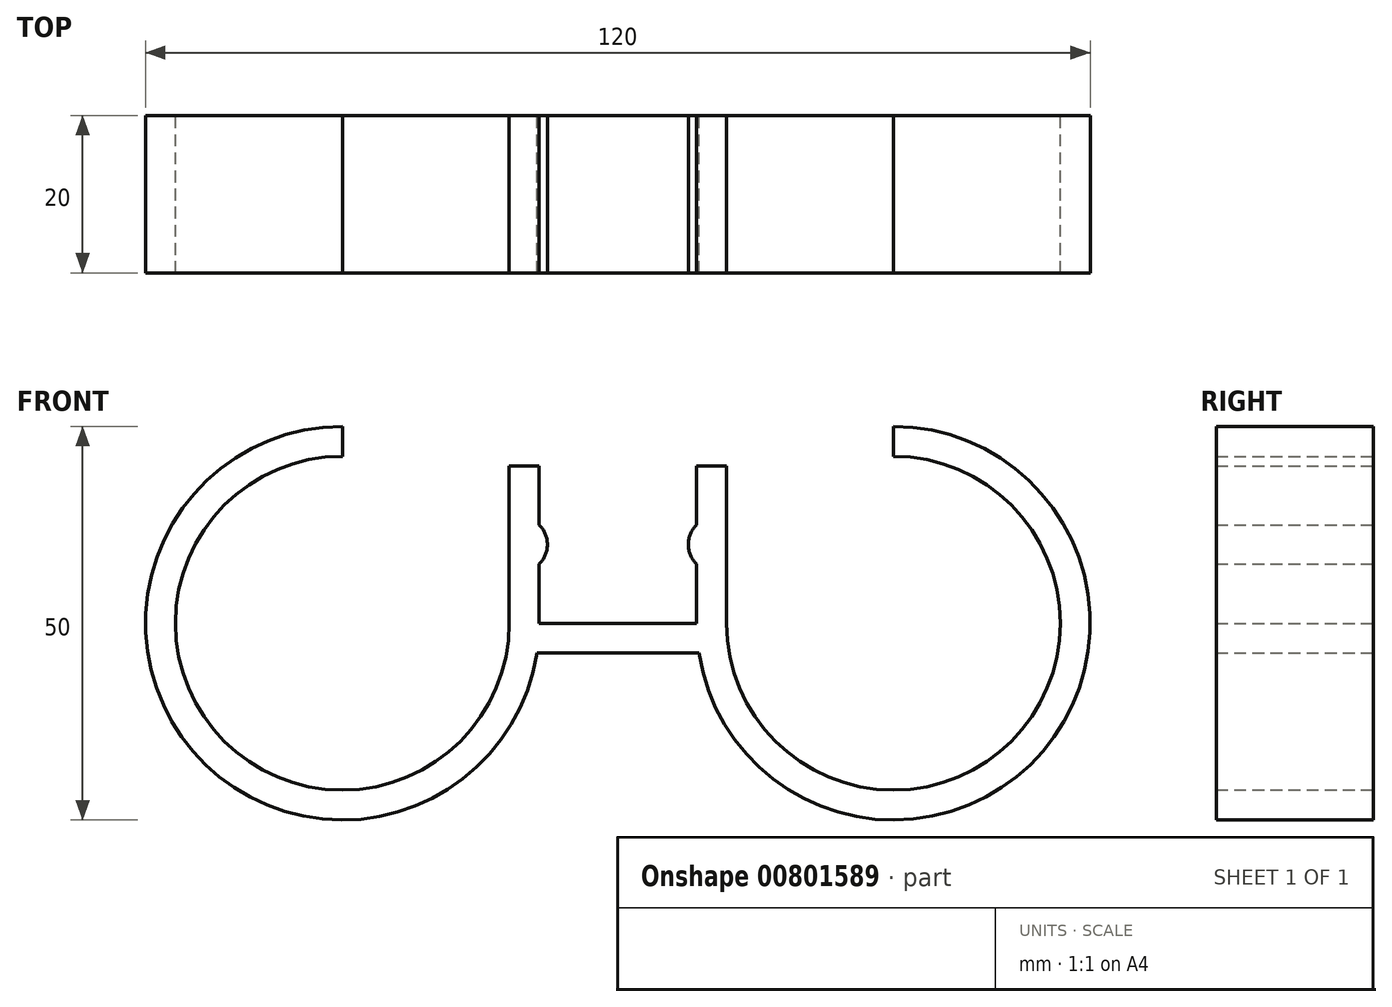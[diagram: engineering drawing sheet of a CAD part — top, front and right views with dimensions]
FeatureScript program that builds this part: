
annotation { "Feature Type Name" : "Feature", "Feature Type Description" : "" }
export const myFeature = defineFeature(function(context is Context, id is Id, definition is map)
    precondition{}
    {
        {
            var Q0;
            Q0=qCreatedBy(makeId("Front.planeOp"),FACE);
            var sketch = newSketch(context, id + "F0", { "sketchPlane" : qUnion([Q0])});
            skLineSegment(sketch, "E0.bottom", {"start": v(10, -10) * mm, "end": v(-10, -10) * mm, "construction": true});
            skLineSegment(sketch, "E0.top", {"start": v(10, 10) * mm, "end": v(-10, 10) * mm, "construction": true});
            skLineSegment(sketch, "E0.left", {"start": v(10, -10) * mm, "end": v(10, 10) * mm, "construction": true});
            skLineSegment(sketch, "E0.right", {"start": v(-10, -10) * mm, "end": v(-10, 10) * mm, "construction": true});
            skPoint(sketch, "E0.middle", {"position": v(0, 0) * mm});
            skLineSegment(sketch, "E1", {"start": v(-10, -2.5) * mm, "end": v(-8.5, -2.5) * mm, "construction": true});
            skLineSegment(sketch, "E2", {"start": v(-10, 2.5) * mm, "end": v(-8.5, 2.5) * mm, "construction": true});
            skLineSegment(sketch, "E3.bottom", {"start": v(4, -4) * mm, "end": v(-4, -4) * mm});
            skLineSegment(sketch, "E3.top", {"start": v(4, 4) * mm, "end": v(-4, 4) * mm, "construction": true});
            skLineSegment(sketch, "E3.left", {"start": v(4, -4) * mm, "end": v(4, 4) * mm, "construction": true});
            skLineSegment(sketch, "E3.right", {"start": v(-4, -4) * mm, "end": v(-4, 4) * mm, "construction": true});
            skArc(sketch, "E4", {"start": v(-35, 15) * mm, "mid": v(-53.97, -26.28) * mm, "end": v(-10.3, -13.8) * mm});
            skPoint(sketch, "E5", {"position": v(-10, 0) * mm});
            skLineSegment(sketch, "E6", {"start": v(-10, 10) * mm, "end": v(-10, 2.5) * mm});
            skLineSegment(sketch, "E7.0", {"start": v(-13.8, 10) * mm, "end": v(-13.8, -10) * mm});
            skArc(sketch, "E8.0", {"start": v(-35, 11.2) * mm, "mid": v(-50, -25) * mm, "end": v(-13.8, -10) * mm});
            skLineSegment(sketch, "E9", {"start": v(-10, -10) * mm, "end": v(0, -10) * mm});
            skLineSegment(sketch, "E10", {"start": v(0, -10) * mm, "end": v(0, -13.8) * mm});
            skLineSegment(sketch, "E11", {"start": v(0, -13.8) * mm, "end": v(-10.3, -13.8) * mm});
            skLineSegment(sketch, "E12", {"start": v(-13.8, 10) * mm, "end": v(-10, 10) * mm});
            skLineSegment(sketch, "E13", {"start": v(-35, 11.2) * mm, "end": v(-35, 15) * mm});
            skLineSegment(sketch, "E14.MirrorCS", {"start": v(-13.8, 10) * mm, "end": v(-17.6, 10) * mm});
            skLineSegment(sketch, "E15.MirrorCS", {"start": v(-17.6, 10) * mm, "end": v(-17.6, -10) * mm});
            skLineSegment(sketch, "E16.MirrorCS", {"start": v(10, 10) * mm, "end": v(10, 2.5) * mm});
            skLineSegment(sketch, "E17.MirrorCS", {"start": v(13.8, 10) * mm, "end": v(10, 10) * mm});
            skLineSegment(sketch, "E18.MirrorCS", {"start": v(13.8, 10) * mm, "end": v(13.8, -10) * mm});
            skLineSegment(sketch, "E19.MirrorCS", {"start": v(0, -13.8) * mm, "end": v(10.3, -13.8) * mm});
            skLineSegment(sketch, "E20.MirrorCS", {"start": v(10, -10) * mm, "end": v(0, -10) * mm});
            skArc(sketch, "E21.MirrorCS", {"start": v(35, 15) * mm, "mid": v(53.97, -26.28) * mm, "end": v(10.3, -13.8) * mm});
            skArc(sketch, "E22.MirrorCS", {"start": v(35, 11.2) * mm, "mid": v(50, -25) * mm, "end": v(13.8, -10) * mm});
            skLineSegment(sketch, "E23.MirrorCS", {"start": v(35, 11.2) * mm, "end": v(35, 15) * mm});
            skArc(sketch, "E24", {"start": v(-10, -2.5) * mm, "mid": v(-8.95, 0) * mm, "end": v(-10, 2.5) * mm});
            skLineSegment(sketch, "E25.trimOffspring", {"start": v(-10, -2.5) * mm, "end": v(-10, -10) * mm});
            skArc(sketch, "E26.MirrorCS", {"start": v(10, -2.5) * mm, "mid": v(8.95, 0) * mm, "end": v(10, 2.5) * mm});
            skLineSegment(sketch, "E27.trimOffspring", {"start": v(10, -2.5) * mm, "end": v(10, -10) * mm});
            skSolve(sketch);
        }
        {
            var Q0;
            Q0 = qSketchRegion(id + "F0", true);
            extrude(context, id + "F1", {"entities" : qUnion([Q0]), "endBound" : BoundingType.SYMMETRIC, "depth" : 20 * mm, "offsetDistance" : 25 * mm});
        }
    });
